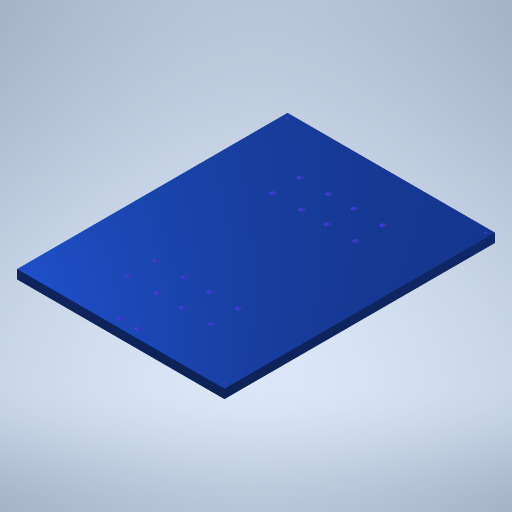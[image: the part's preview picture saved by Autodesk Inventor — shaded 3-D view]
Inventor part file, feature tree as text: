
AUTODESK INVENTOR PART (.ipt)
format: ipt  version: 2024 (Build 280153000, 153)  size: 303,616 bytes
history: native  units: mm
features: other x4, extrude x1, sketch x1
ambient origin geometry x8: Origin, YZ Plane, XZ Plane, XY Plane, X Axis, Y Axis, Z Axis, Center Point
bodies: Solido1 (feature_tree)
feature tree (6):
  extrude  "Estrusione1"  Depth=300.0mm
  sketch  "Schizzo1"
  other  "Finish1"
  other  "Finish2"
  other  "Finish3"
  other  "Finish4"
